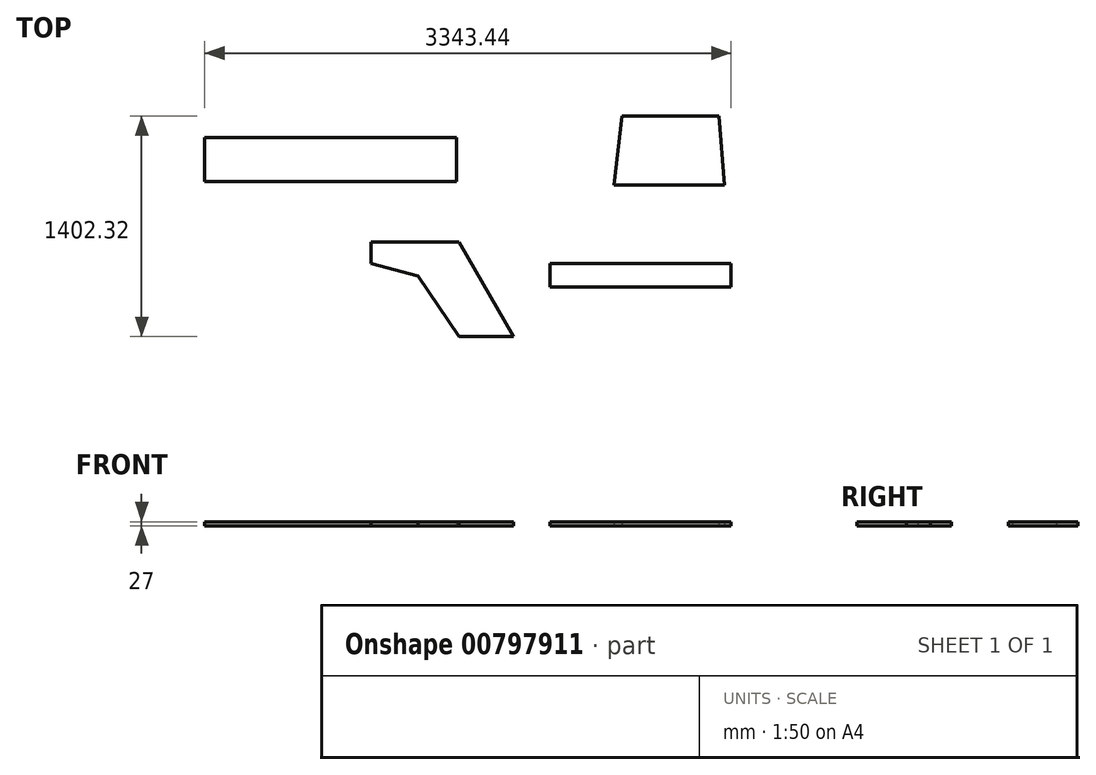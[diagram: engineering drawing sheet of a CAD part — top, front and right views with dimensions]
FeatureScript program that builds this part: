
annotation { "Feature Type Name" : "Feature", "Feature Type Description" : "" }
export const myFeature = defineFeature(function(context is Context, id is Id, definition is map)
    precondition{}
    {
        {
            assignVariable(context, id + "F0", {"name" : "thickness", "anyValue" : 27});
        }
        {
            var Q0;
            Q0=qCreatedBy(makeId("Top.planeOp"),FACE);
            var sketch = newSketch(context, id + "F1", { "sketchPlane" : qUnion([Q0])});
            skLineSegment(sketch, "E0.bottom", {"start": v(-2333.94, 303.16) * mm, "end": v(-733.94, 303.16) * mm});
            skLineSegment(sketch, "E0.top", {"start": v(-2333.94, 23.16) * mm, "end": v(-733.94, 23.16) * mm});
            skLineSegment(sketch, "E0.left", {"start": v(-2333.94, 303.16) * mm, "end": v(-2333.94, 23.16) * mm});
            skLineSegment(sketch, "E0.right", {"start": v(-733.94, 303.16) * mm, "end": v(-733.94, 23.16) * mm});
            skSolve(sketch);
        }
        {
            var Q0;
            Q0 = qSketchRegion(id + "F1", true);
            extrude(context, id + "F2", {"entities" : qUnion([Q0]), "depth" : 27 * mm, "offsetDistance" : 25 * mm});
        }
        {
            var Q0;
            Q0=qCreatedBy(makeId("Top.planeOp"),FACE);
            var sketch = newSketch(context, id + "F3", { "sketchPlane" : qUnion([Q0])});
            skLineSegment(sketch, "E1.bottom", {"start": v(-140.5, -498.1) * mm, "end": v(1009.5, -498.1) * mm});
            skLineSegment(sketch, "E1.top", {"start": v(-140.5, -648.1) * mm, "end": v(1009.5, -648.1) * mm});
            skLineSegment(sketch, "E1.left", {"start": v(-140.5, -498.1) * mm, "end": v(-140.5, -648.1) * mm});
            skLineSegment(sketch, "E1.right", {"start": v(1009.5, -498.1) * mm, "end": v(1009.5, -648.1) * mm});
            skSolve(sketch);
        }
        {
            var Q0;
            Q0 = qSketchRegion(id + "F3", true);
            extrude(context, id + "F4", {"entities" : qUnion([Q0]), "depth" : 27 * mm, "offsetDistance" : 25 * mm});
        }
        {
            var Q0;
            Q0=qCreatedBy(makeId("Top.planeOp"),FACE);
            var sketch = newSketch(context, id + "F5", { "sketchPlane" : qUnion([Q0])});
            skLineSegment(sketch, "E2.bottom", {"start": v(-1278.8, -362.32) * mm, "end": v(-718.8, -362.32) * mm});
            skLineSegment(sketch, "E2.top", {"start": v(-1278.8, -962.32) * mm, "end": v(-718.8, -962.32) * mm});
            skLineSegment(sketch, "E2.left", {"start": v(-1278.8, -362.32) * mm, "end": v(-1278.8, -962.32) * mm});
            skLineSegment(sketch, "E2.right", {"start": v(-718.8, -362.32) * mm, "end": v(-718.8, -962.32) * mm});
            skLineSegment(sketch, "E3", {"start": v(-1278.8, -498.14) * mm, "end": v(-978.7, -575.26) * mm});
            skLineSegment(sketch, "E4", {"start": v(-978.7, -575.26) * mm, "end": v(-718.8, -962.32) * mm});
            skLineSegment(sketch, "E5", {"start": v(-718.8, -362.32) * mm, "end": v(-372.38, -962.32) * mm});
            skLineSegment(sketch, "E6", {"start": v(-372.38, -962.32) * mm, "end": v(-718.8, -962.32) * mm});
            skSolve(sketch);
        }
        {
            var Q0;
            {var subQ1=sQuery(id+"F5.wireOp",EDGE,"E2.bottom");Q0=makeQuery(id+"F5.imprint","IMPRINT",FACE,{"disambiguationData":[TD([[makeQuery(id+"F5.imprint","IMPRINT",EDGE,{"derivedFrom":subQ1}),-1.0]])]});}
            var Q1;
            Q1=makeQuery(id+"F5.imprint","IMPRINT",FACE,{"disambiguationData":[TD([[makeQuery(id+"F5.imprint","IMPRINT",EDGE,{"derivedFrom":sQuery(id+"F5.wireOp",EDGE,"E2.right")}),1.0]])]});
            extrude(context, id + "F6", {"entities" : qUnion([Q0, Q1]), "depth" : 27 * mm, "offsetDistance" : 25 * mm});
        }
        {
            var Q0;
            Q0=qCreatedBy(makeId("Top.planeOp"),FACE);
            var sketch = newSketch(context, id + "F7", { "sketchPlane" : qUnion([Q0])});
            skLineSegment(sketch, "E7.bottom", {"start": v(265.72, 440) * mm, "end": v(965.72, 440) * mm});
            skLineSegment(sketch, "E7.top", {"start": v(265.72, 0) * mm, "end": v(965.72, 0) * mm});
            skLineSegment(sketch, "E7.left", {"start": v(265.72, 440) * mm, "end": v(265.72, 0) * mm});
            skLineSegment(sketch, "E7.right", {"start": v(965.72, 440) * mm, "end": v(965.72, 0) * mm});
            skLineSegment(sketch, "E8", {"start": v(317.15, 440) * mm, "end": v(265.72, 0) * mm});
            skLineSegment(sketch, "E9", {"start": v(965.72, 0) * mm, "end": v(931.15, 440) * mm});
            skSolve(sketch);
        }
        {
            var Q0;
            Q0=makeQuery(id+"F7.imprint","IMPRINT",FACE,{"disambiguationData":[TD([[makeQuery(id+"F7.imprint","IMPRINT",EDGE,{"derivedFrom":sQuery(id+"F7.wireOp",EDGE,"E7.top")}),1.0]])]});
            extrude(context, id + "F8", {"entities" : qUnion([Q0]), "depth" : (getVariable(context, 'thickness')) * mm, "offsetDistance" : 25 * mm});
        }
    });
